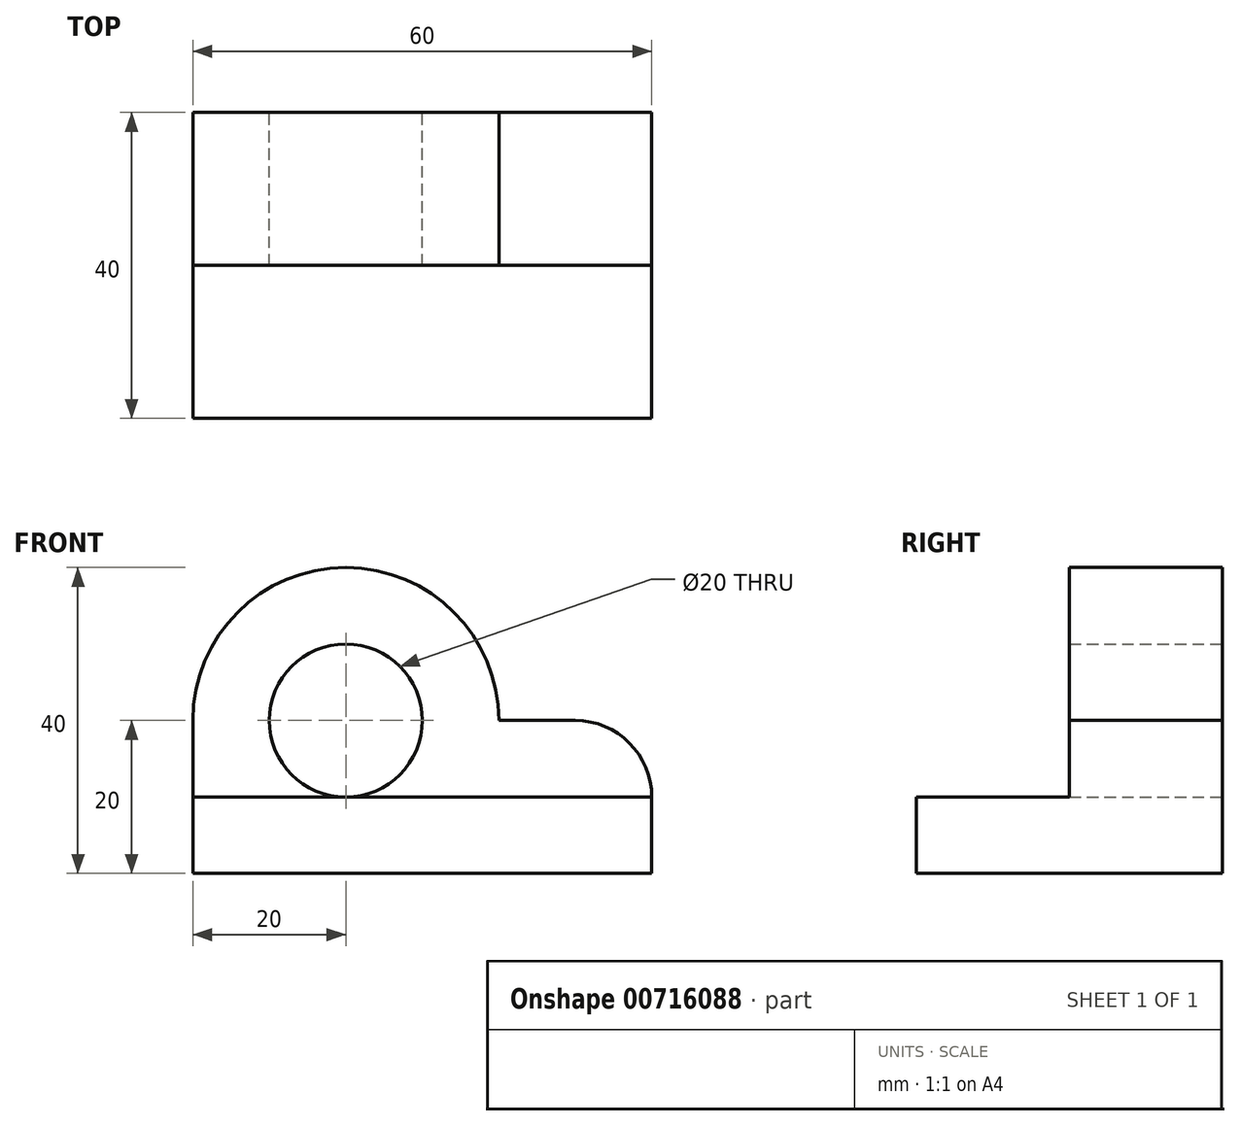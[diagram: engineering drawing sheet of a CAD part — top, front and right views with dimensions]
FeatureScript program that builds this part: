
annotation { "Feature Type Name" : "Feature", "Feature Type Description" : "" }
export const myFeature = defineFeature(function(context is Context, id is Id, definition is map)
    precondition{}
    {
        {
            var Q0;
            Q0=qCreatedBy(makeId("Front.planeOp"),FACE);
            var sketch = newSketch(context, id + "F0", { "sketchPlane" : qUnion([Q0])});
            skLineSegment(sketch, "E0", {"start": v(0, 0) * mm, "end": v(0, 10) * mm});
            skLineSegment(sketch, "E1", {"start": v(0, 0) * mm, "end": v(60, 0) * mm});
            skLineSegment(sketch, "E2", {"start": v(60, 0) * mm, "end": v(60, 10) * mm});
            skLineSegment(sketch, "E3", {"start": v(60, 10) * mm, "end": v(0, 10) * mm});
            skLineSegment(sketch, "E4", {"start": v(0, 10) * mm, "end": v(0, 20) * mm});
            skLineSegment(sketch, "E5", {"start": v(60, 10) * mm, "end": v(60, 10) * mm});
            skLineSegment(sketch, "E6", {"start": v(50, 20) * mm, "end": v(40, 20) * mm});
            skPoint(sketch, "E7.visualSharp", {"position": v(60, 20) * mm});
            skArc(sketch, "E7.filletArc", {"start": v(60, 10) * mm, "mid": v(57.07, 17.07) * mm, "end": v(50, 20) * mm});
            skLineSegment(sketch, "E8", {"start": v(40, 20) * mm, "end": v(0, 20) * mm});
            skLineSegment(sketch, "E9", {"start": v(40, 20) * mm, "end": v(20, 20) * mm});
            skCircle(sketch, "E10", {"center": v(20, 20) * mm, "radius": 20 * mm});
            skCircle(sketch, "E11", {"center": v(20, 20) * mm, "radius": 10 * mm});
            skSolve(sketch);
        }
        {
            var Q0;
            {var subQ0=sQuery(id+"F0.wireOp",EDGE,"E2");Q0=makeQuery(id+"F0.imprint","IMPRINT",FACE,{"disambiguationData":[TD([[makeQuery(id+"F0.imprint","IMPRINT",EDGE,{"derivedFrom":subQ0}),1.0]])]});}
            var Q1;
            {var subQ0=sQuery(id+"F0.wireOp",EDGE,"E0");Q1=makeQuery(id+"F0.imprint","IMPRINT",FACE,{"disambiguationData":[TD([[makeQuery(id+"F0.imprint","IMPRINT",EDGE,{"derivedFrom":subQ0}),-1.0]])]});}
            var Q2;
            {var subQ0=sQuery(id+"F0.wireOp",EDGE,"E10");var subQ1=sQuery(id+"F0.wireOp",EDGE,"E3");var subQ2=makeQuery(id+"F0.imprint","INTERSECT",VERTEX,{"disambiguationData":[OD(0.0)],"derivedFrom":[subQ1,subQ0]});Q2=makeQuery(id+"F0.imprint","IMPRINT",FACE,{"disambiguationData":[TD([[makeQuery(id+"F0.imprint","IMPRINT",EDGE,{"disambiguationData":[TD([[subQ2,-1.0]])],"derivedFrom":subQ1}),1.0]])]});}
            extrude(context, id + "F1", {"entities" : qUnion([Q0, Q1, Q2]), "depth" : 40 * mm, "offsetDistance" : 25 * mm});
        }
        {
            var Q0;
            Q0 = qSketchRegion(id + "F0", true);
            extrude(context, id + "F2", {"entities" : qUnion([Q0]), "operationType" : NewBodyOperationType.ADD, "depth" : 20 * mm, "offsetDistance" : 25 * mm});
        }
    });
